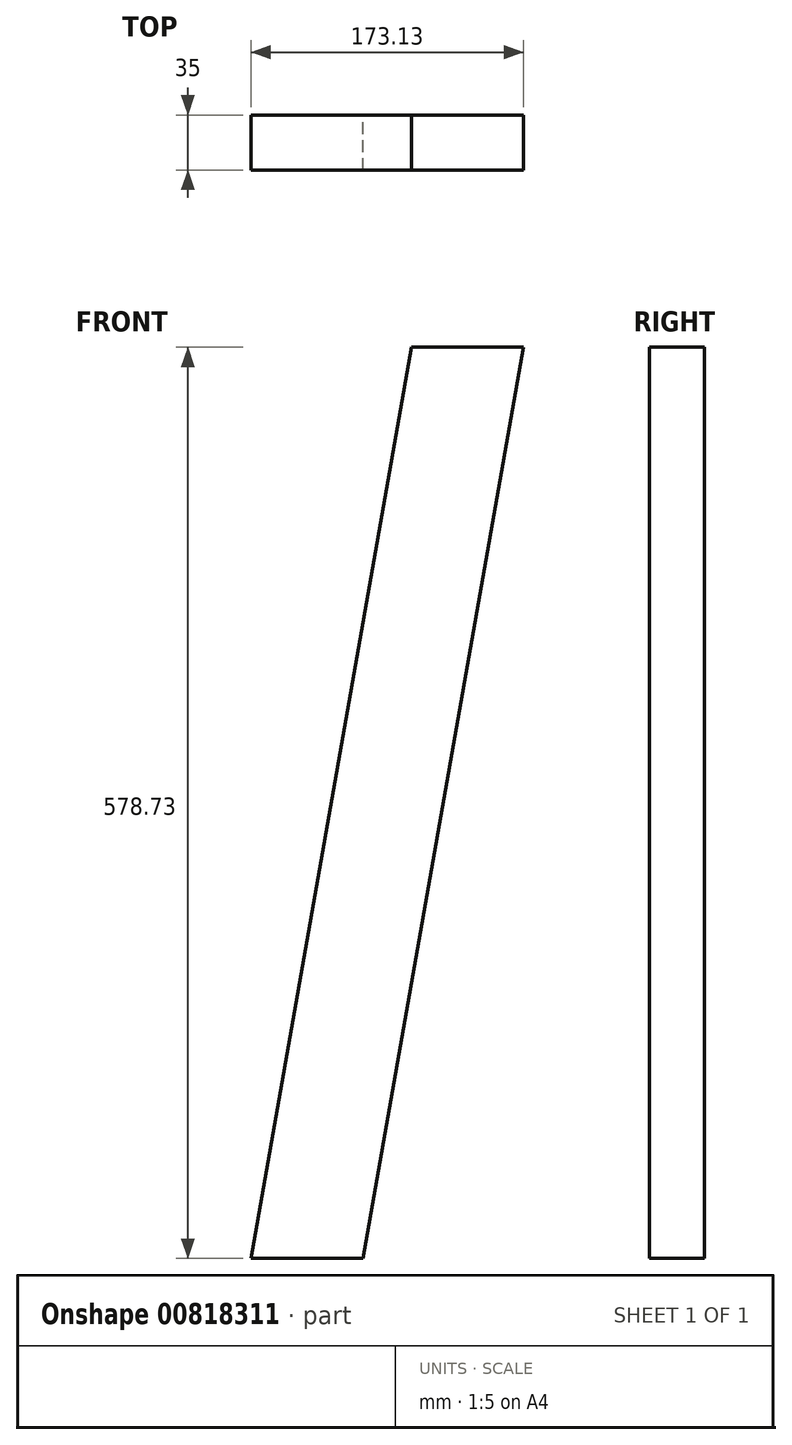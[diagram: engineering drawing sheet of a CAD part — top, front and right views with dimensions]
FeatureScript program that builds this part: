
annotation { "Feature Type Name" : "Feature", "Feature Type Description" : "" }
export const myFeature = defineFeature(function(context is Context, id is Id, definition is map)
    precondition{}
    {
        {
            var Q0;
            Q0=qCreatedBy(makeId("Front.planeOp"),FACE);
            var sketch = newSketch(context, id + "F0", { "sketchPlane" : qUnion([Q0])});
            skLineSegment(sketch, "E0.left", {"start": v(102.05, 578.73) * mm, "end": v(0, 0) * mm});
            skLineSegment(sketch, "E0.right", {"start": v(173.13, 578.73) * mm, "end": v(71.08, 0) * mm});
            skPoint(sketch, "E1", {"position": v(70.53, 400) * mm});
            skLineSegment(sketch, "E2", {"start": v(71.08, 0) * mm, "end": v(0, 0) * mm});
            skLineSegment(sketch, "E3", {"start": v(173.13, 578.73) * mm, "end": v(102.05, 578.73) * mm});
            skSolve(sketch);
        }
        {
            var Q0;
            Q0 = qSketchRegion(id + "F0", true);
            extrude(context, id + "F1", {"entities" : qUnion([Q0]), "depth" : 35 * mm, "offsetDistance" : 25 * mm});
        }
    });
